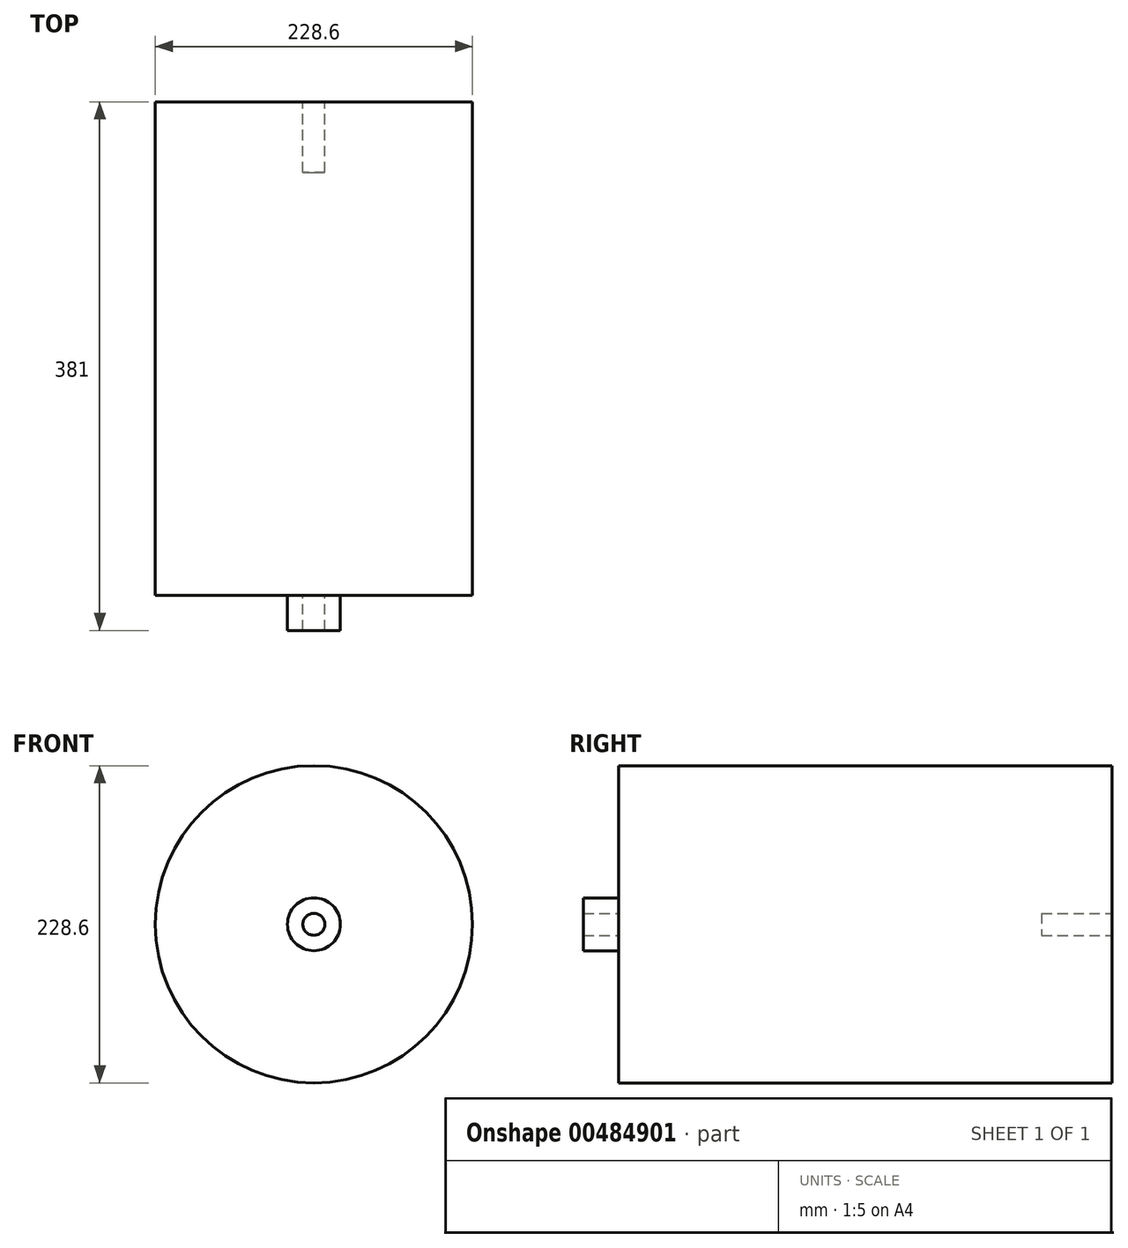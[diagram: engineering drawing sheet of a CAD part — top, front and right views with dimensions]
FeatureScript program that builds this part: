
annotation { "Feature Type Name" : "Feature", "Feature Type Description" : "" }
export const myFeature = defineFeature(function(context is Context, id is Id, definition is map)
    precondition{}
    {
        {
            var Q0;
            Q0=qCreatedBy(makeId("Front.planeOp"),FACE);
            var sketch = newSketch(context, id + "F0", { "sketchPlane" : qUnion([Q0])});
            skCircle(sketch, "E0", {"center": v(0, 0) * mm, "radius": 19.05 * mm});
            skCircle(sketch, "E1", {"center": v(0, 0) * mm, "radius": 7.94 * mm});
            skSolve(sketch);
        }
        {
            var Q0;
            Q0 = qSketchRegion(id + "F0", true);
            extrude(context, id + "F1", {"entities" : qUnion([Q0]), "depth" : 25.4 * mm});
        }
        {
            var Q0;
            Q0=qCreatedBy(makeId("Front.planeOp"),FACE);
            var sketch = newSketch(context, id + "F2", { "sketchPlane" : qUnion([Q0])});
            skCircle(sketch, "E2", {"center": v(0, 0) * mm, "radius": 114.3 * mm});
            skSolve(sketch);
        }
        {
            var Q0;
            Q0 = qSketchRegion(id + "F2", true);
            extrude(context, id + "F3", {"entities" : qUnion([Q0]), "oppositeDirection" : true, "depth" : 355.6 * mm});
        }
        {
            var Q0;
            Q0=makeQuery(id+"F3.opExtrude","CAP_FACE",FACE,{"disambiguationData":[OSD([sQuery(id+"F2.wireOp",EDGE,"E2")])],"isStart":false});
            var sketch = newSketch(context, id + "F4", { "sketchPlane" : qUnion([Q0])});
            skCircle(sketch, "E3", {"center": v(0, 0) * mm, "radius": 7.94 * mm});
            skSolve(sketch);
        }
        {
            var Q0;
            Q0 = qSketchRegion(id + "F4", true);
            extrude(context, id + "F5", {"entities" : qUnion([Q0]), "operationType" : NewBodyOperationType.REMOVE, "oppositeDirection" : true, "depth" : 50.8 * mm});
        }
        {
            var Q0;
            Q0=makeQuery(id+"F3.opExtrude","CAP_FACE",FACE,{"disambiguationData":[OSD([sQuery(id+"F2.wireOp",EDGE,"E2")])],"isStart":false});
            var sketch = newSketch(context, id + "F6", { "sketchPlane" : qUnion([Q0])});
            skCircle(sketch, "E4", {"center": v(0, 0) * mm, "radius": 114.3 * mm});
            skPoint(sketch, "E4.first.point", {"position": v(35.8, -108.55) * mm});
            skPoint(sketch, "E4.second.point", {"position": v(-110.7, 28.44) * mm});
            skPoint(sketch, "E4.third.point", {"position": v(68.52, 91.48) * mm});
            skSolve(sketch);
        }
        {
            var Q0;
            Q0 = qSketchRegion(id + "F6", true);
            extrude(context, id + "F7", {"entities" : qUnion([Q0]), "depth" : 50.8 * mm});
        }
        {
            var Q0;
            Q0=makeQuery(id+"F7.opExtrude","SWEPT_BODY",BODY,{"disambiguationData":[OSD([sQuery(id+"F6.wireOp",EDGE,"E4")])]});
            deleteBodies(context, id + "F8", {"entities" : qUnion([Q0])});
        }
    });
